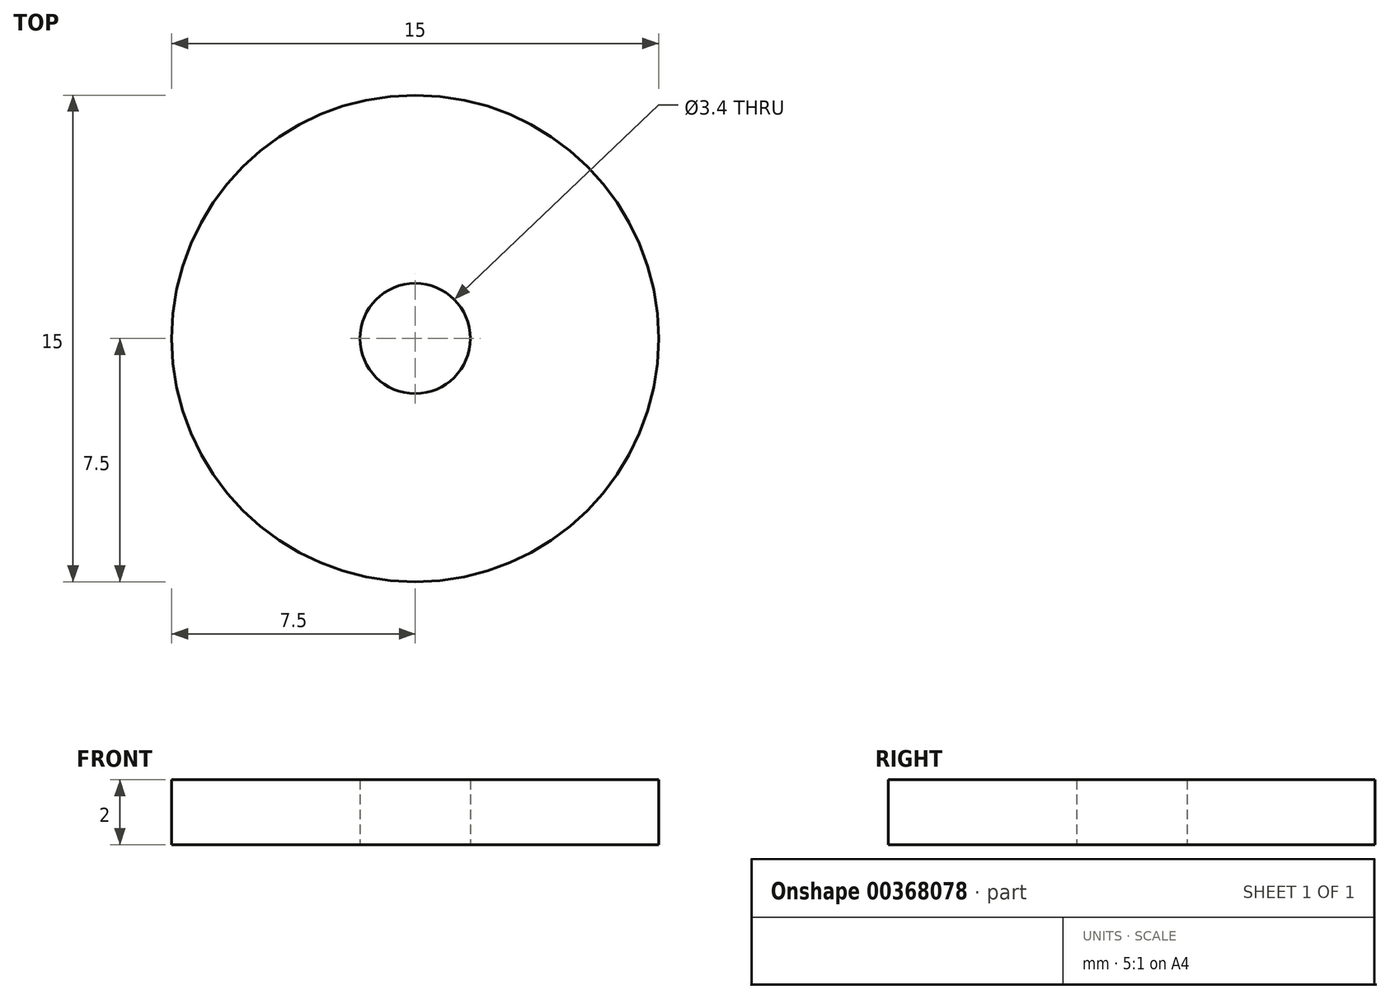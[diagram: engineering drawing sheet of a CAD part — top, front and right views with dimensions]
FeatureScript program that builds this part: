
annotation { "Feature Type Name" : "Feature", "Feature Type Description" : "" }
export const myFeature = defineFeature(function(context is Context, id is Id, definition is map)
    precondition{}
    {
        {
            var Q0;
            Q0=qCreatedBy(makeId("Top.planeOp"),FACE);
            var sketch = newSketch(context, id + "F0", { "sketchPlane" : qUnion([Q0])});
            skCircle(sketch, "E0", {"center": v(0, 0) * mm, "radius": 7.5 * mm});
            skCircle(sketch, "E1", {"center": v(0, 0) * mm, "radius": 1.7 * mm});
            skSolve(sketch);
        }
        {
            var Q0;
            Q0=makeQuery(id+"F0.imprint","IMPRINT",FACE,{"disambiguationData":[TD([[makeQuery(id+"F0.imprint","IMPRINT",EDGE,{"derivedFrom":sQuery(id+"F0.wireOp",EDGE,"E0")}),1.0]])]});
            extrude(context, id + "F1", {"entities" : qUnion([Q0]), "depth" : 2 * mm});
        }
    });
